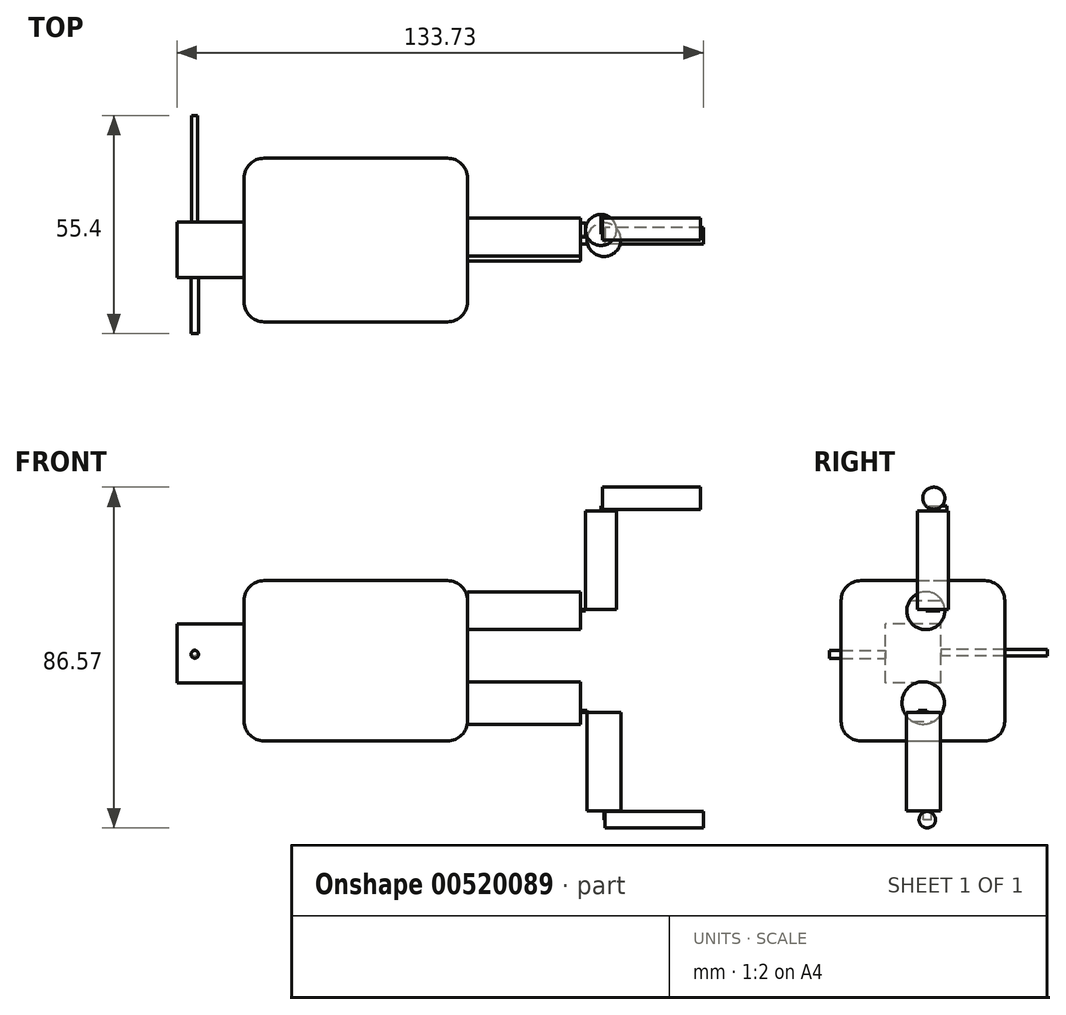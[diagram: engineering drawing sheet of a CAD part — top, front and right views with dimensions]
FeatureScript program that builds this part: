
annotation { "Feature Type Name" : "Feature", "Feature Type Description" : "" }
export const myFeature = defineFeature(function(context is Context, id is Id, definition is map)
    precondition{}
    {
        {
            var Q0;
            Q0=qCreatedBy(makeId("Top.planeOp"),FACE);
            var sketch = newSketch(context, id + "F0", { "sketchPlane" : qUnion([Q0])});
            skLineSegment(sketch, "E0.bottom", {"start": v(-23.58, -17.27) * mm, "end": v(33.13, -17.27) * mm});
            skLineSegment(sketch, "E0.top", {"start": v(-23.58, 24.28) * mm, "end": v(33.13, 24.28) * mm});
            skLineSegment(sketch, "E0.left", {"start": v(-23.58, -17.27) * mm, "end": v(-23.58, 24.28) * mm});
            skLineSegment(sketch, "E0.right", {"start": v(33.13, -17.27) * mm, "end": v(33.13, 24.28) * mm});
            skSolve(sketch);
        }
        {
            var Q0;
            Q0=makeQuery(id+"F0.imprint","IMPRINT",FACE,{"disambiguationData":[TD([[makeQuery(id+"F0.imprint","IMPRINT",EDGE,{"derivedFrom":sQuery(id+"F0.wireOp",EDGE,"E0.bottom")}),1.0]])]});
            extrude(context, id + "F1", {"entities" : qUnion([Q0]), "depth" : 40.7 * mm});
        }
        {
            var Q0;
            Q0=makeQuery(id+"F1.opExtrude","SWEPT_EDGE",EDGE,{"disambiguationData":[OSD([sQuery(id+"F0.wireOp",EDGE,"E0.top"),sQuery(id+"F0.wireOp",EDGE,"E0.left")])]});
            var Q1;
            Q1=makeQuery(id+"F1.opExtrude","CAP_EDGE",EDGE,{"disambiguationData":[OSD([sQuery(id+"F0.wireOp",EDGE,"E0.top")])],"isStart":true});
            var Q2;
            Q2=makeQuery(id+"F1.opExtrude","CAP_EDGE",EDGE,{"disambiguationData":[OSD([sQuery(id+"F0.wireOp",EDGE,"E0.left")])],"isStart":true});
            var Q3;
            Q3=makeQuery(id+"F1.opExtrude","CAP_EDGE",EDGE,{"disambiguationData":[OSD([sQuery(id+"F0.wireOp",EDGE,"E0.top")])],"isStart":false});
            var Q4;
            Q4=makeQuery(id+"F1.opExtrude","SWEPT_EDGE",EDGE,{"disambiguationData":[OSD([sQuery(id+"F0.wireOp",EDGE,"E0.top"),sQuery(id+"F0.wireOp",EDGE,"E0.right")])]});
            var Q5;
            Q5=makeQuery(id+"F1.opExtrude","CAP_EDGE",EDGE,{"disambiguationData":[OSD([sQuery(id+"F0.wireOp",EDGE,"E0.left")])],"isStart":false});
            var Q6;
            Q6=makeQuery(id+"F1.opExtrude","CAP_EDGE",EDGE,{"disambiguationData":[OSD([sQuery(id+"F0.wireOp",EDGE,"E0.right")])],"isStart":false});
            var Q7;
            Q7=makeQuery(id+"F1.opExtrude","SWEPT_EDGE",EDGE,{"disambiguationData":[OSD([sQuery(id+"F0.wireOp",EDGE,"E0.bottom"),sQuery(id+"F0.wireOp",EDGE,"E0.left")])]});
            var Q8;
            Q8=makeQuery(id+"F1.opExtrude","CAP_EDGE",EDGE,{"disambiguationData":[OSD([sQuery(id+"F0.wireOp",EDGE,"E0.bottom")])],"isStart":false});
            var Q9;
            Q9=makeQuery(id+"F1.opExtrude","CAP_EDGE",EDGE,{"disambiguationData":[OSD([sQuery(id+"F0.wireOp",EDGE,"E0.right")])],"isStart":true});
            var Q10;
            Q10=makeQuery(id+"F1.opExtrude","CAP_EDGE",EDGE,{"disambiguationData":[OSD([sQuery(id+"F0.wireOp",EDGE,"E0.bottom")])],"isStart":true});
            var Q11;
            Q11=makeQuery(id+"F1.opExtrude","SWEPT_EDGE",EDGE,{"disambiguationData":[OSD([sQuery(id+"F0.wireOp",EDGE,"E0.bottom"),sQuery(id+"F0.wireOp",EDGE,"E0.right")])]});
            fillet(context, id + "F2", {"entities" : qUnion([Q0, Q1, Q2, Q3, Q4, Q5, Q6, Q7, Q8, Q9, Q10, Q11]), "radius" : 5 * mm, "tangentPropagation" : true, "allowEdgeOverflow" : false});
        }
        {
            var Q0;
            Q0=makeQuery(id+"F1.opExtrude","SWEPT_FACE",FACE,{"disambiguationData":[OSD([sQuery(id+"F0.wireOp",EDGE,"E0.left")])]});
            var sketch = newSketch(context, id + "F3", { "sketchPlane" : qUnion([Q0])});
            skLineSegment(sketch, "E1.bottom", {"start": v(-8.11, 14.74) * mm, "end": v(5.98, 14.74) * mm});
            skLineSegment(sketch, "E1.top", {"start": v(-8.11, 29.69) * mm, "end": v(5.98, 29.69) * mm});
            skLineSegment(sketch, "E1.left", {"start": v(-8.11, 14.74) * mm, "end": v(-8.11, 29.69) * mm});
            skLineSegment(sketch, "E1.right", {"start": v(5.98, 14.74) * mm, "end": v(5.98, 29.69) * mm});
            skSolve(sketch);
        }
        {
            var Q0;
            Q0=makeQuery(id+"F3.imprint","IMPRINT",FACE,{"disambiguationData":[TD([[makeQuery(id+"F3.imprint","IMPRINT",EDGE,{"derivedFrom":sQuery(id+"F3.wireOp",EDGE,"E1.bottom")}),1.0]])]});
            extrude(context, id + "F4", {"entities" : qUnion([Q0]), "operationType" : NewBodyOperationType.ADD, "depth" : 17.1 * mm});
        }
        {
            var Q0;
            Q0=makeQuery(id+"F4.opExtrude","SWEPT_FACE",FACE,{"disambiguationData":[OSD([sQuery(id+"F3.wireOp",EDGE,"E1.right")])]});
            var sketch = newSketch(context, id + "F5", { "sketchPlane" : qUnion([Q0])});
            skCircle(sketch, "E2", {"center": v(-36.21, 22.4) * mm, "radius": 0.8 * mm});
            skSolve(sketch);
        }
        {
            var Q0;
            Q0=makeQuery(id+"F5.imprint","IMPRINT",FACE,{"disambiguationData":[TD([[makeQuery(id+"F5.imprint","IMPRINT",EDGE,{"derivedFrom":sQuery(id+"F5.wireOp",EDGE,"E2")}),1.0]])]});
            extrude(context, id + "F6", {"entities" : qUnion([Q0]), "operationType" : NewBodyOperationType.ADD, "oppositeDirection" : true, "depth" : 41.1 * mm});
        }
        {
            var Q0;
            Q0=makeQuery(id+"F4.opExtrude","SWEPT_FACE",FACE,{"disambiguationData":[OSD([sQuery(id+"F3.wireOp",EDGE,"E1.right")])]});
            var sketch = newSketch(context, id + "F7", { "sketchPlane" : qUnion([Q0])});
            skCircle(sketch, "E3", {"center": v(-36.13, 21.96) * mm, "radius": 0.97 * mm});
            skSolve(sketch);
        }
        {
            var Q0;
            Q0=makeQuery(id+"F7.imprint","IMPRINT",FACE,{"disambiguationData":[TD([[makeQuery(id+"F7.imprint","IMPRINT",EDGE,{"derivedFrom":sQuery(id+"F7.wireOp",EDGE,"E3")}),1.0]])]});
            extrude(context, id + "F8", {"entities" : qUnion([Q0]), "operationType" : NewBodyOperationType.ADD, "depth" : 14.3 * mm});
        }
        {
            var Q0;
            Q0=makeQuery(id+"F8.opExtrude","CAP_FACE",FACE,{"disambiguationData":[OSD([sQuery(id+"F7.wireOp",EDGE,"E3")])],"isStart":false});
            var sketch = newSketch(context, id + "F9", { "sketchPlane" : qUnion([Q0])});
            skArc(sketch, "E4", {"start": v(-36.1, 22.93) * mm, "mid": v(-44.04, 23.01) * mm, "end": v(-36.35, 21.02) * mm});
            skSolve(sketch);
        }
        {
            var Q0;
            Q0=makeQuery(id+"F1.opExtrude","SWEPT_FACE",FACE,{"disambiguationData":[OSD([sQuery(id+"F0.wireOp",EDGE,"E0.right")])]});
            var sketch = newSketch(context, id + "F10", { "sketchPlane" : qUnion([Q0])});
            skCircle(sketch, "E5", {"center": v(4.26, 33.07) * mm, "radius": 4.81 * mm});
            skCircle(sketch, "E6", {"center": v(3.57, 9.63) * mm, "radius": 5.4 * mm});
            skSolve(sketch);
        }
        {
            var Q0;
            Q0=qSketchRegion(id+"F10",true);
            extrude(context, id + "F11", {"entities" : qUnion([Q0]), "operationType" : NewBodyOperationType.ADD, "depth" : 28.7 * mm});
        }
        {
            var Q0;
            Q0=makeQuery(id+"F11.opExtrude","CAP_FACE",FACE,{"disambiguationData":[OSD([sQuery(id+"F10.wireOp",EDGE,"E5")])],"isStart":false});
            var sketch = newSketch(context, id + "F12", { "sketchPlane" : qUnion([Q0])});
            skLineSegment(sketch, "E7.bottom", {"start": v(4.26, 33.07) * mm, "end": v(7.84, 33.07) * mm});
            skLineSegment(sketch, "E7.top", {"start": v(4.26, 33.43) * mm, "end": v(7.84, 33.43) * mm});
            skLineSegment(sketch, "E7.left", {"start": v(4.26, 33.07) * mm, "end": v(4.26, 33.43) * mm});
            skLineSegment(sketch, "E7.right", {"start": v(7.84, 33.07) * mm, "end": v(7.84, 33.43) * mm});
            skSolve(sketch);
        }
        {
            var Q0;
            Q0=qSketchRegion(id+"F12",true);
            extrude(context, id + "F13", {"entities" : qUnion([Q0]), "operationType" : NewBodyOperationType.ADD, "depth" : 1.3 * mm});
        }
        {
            var Q0;
            Q0=makeQuery(id+"F13.opExtrude","SWEPT_FACE",FACE,{"disambiguationData":[OSD([sQuery(id+"F12.wireOp",EDGE,"E7.top")])]});
            var sketch = newSketch(context, id + "F14", { "sketchPlane" : qUnion([Q0])});
            skCircle(sketch, "E8", {"center": v(67.07, 6.05) * mm, "radius": 3.94 * mm});
            skPoint(sketch, "E8.first.point", {"position": v(63.13, 6.05) * mm});
            skPoint(sketch, "E8.second.point", {"position": v(71, 6.05) * mm});
            skPoint(sketch, "E8.second.point.positionSnap0", {"position": v(63.13, 6.05) * mm});
            skPoint(sketch, "E8.third.point", {"position": v(68.36, 9.77) * mm});
            skSolve(sketch);
        }
        {
            var Q0;
            Q0=qSketchRegion(id+"F14",true);
            extrude(context, id + "F15", {"entities" : qUnion([Q0]), "depth" : 25 * mm});
        }
        {
            var Q0;
            Q0=makeQuery(id+"F11.opExtrude","CAP_FACE",FACE,{"disambiguationData":[OSD([sQuery(id+"F10.wireOp",EDGE,"E6")])],"isStart":false});
            var sketch = newSketch(context, id + "F16", { "sketchPlane" : qUnion([Q0])});
            skLineSegment(sketch, "E9.bottom", {"start": v(2.43, 7.17) * mm, "end": v(4.59, 7.17) * mm});
            skLineSegment(sketch, "E9.top", {"start": v(2.43, 7.74) * mm, "end": v(4.59, 7.74) * mm});
            skLineSegment(sketch, "E9.left", {"start": v(2.43, 7.17) * mm, "end": v(2.43, 7.74) * mm});
            skLineSegment(sketch, "E9.right", {"start": v(4.59, 7.17) * mm, "end": v(4.59, 7.74) * mm});
            skSolve(sketch);
        }
        {
            var Q0;
            Q0=qSketchRegion(id+"F16",true);
            extrude(context, id + "F17", {"entities" : qUnion([Q0]), "operationType" : NewBodyOperationType.ADD, "depth" : 1.7 * mm});
        }
        {
            var Q0;
            Q0=makeQuery(id+"F17.opExtrude","SWEPT_FACE",FACE,{"disambiguationData":[OSD([sQuery(id+"F16.wireOp",EDGE,"E9.bottom")])]});
            var sketch = newSketch(context, id + "F18", { "sketchPlane" : qUnion([Q0])});
            skCircle(sketch, "E10", {"center": v(67.82, -3.61) * mm, "radius": 4.3 * mm});
            skPoint(sketch, "E10.first.point", {"position": v(63.53, -3.5) * mm});
            skPoint(sketch, "E10.second.point", {"position": v(72.1, -3.5) * mm});
            skPoint(sketch, "E10.second.point.positionSnap0", {"position": v(63.53, -3.5) * mm});
            skPoint(sketch, "E10.third.point", {"position": v(68.95, 0.53) * mm});
            skSolve(sketch);
        }
        {
            var Q0;
            Q0=qSketchRegion(id+"F18",true);
            extrude(context, id + "F19", {"entities" : qUnion([Q0]), "operationType" : NewBodyOperationType.ADD, "depth" : 25 * mm});
        }
        {
            var Q0;
            Q0=makeQuery(id+"F19.opExtrude","CAP_FACE",FACE,{"disambiguationData":[OSD([sQuery(id+"F18.wireOp",EDGE,"E10")])],"isStart":false});
            var sketch = newSketch(context, id + "F20", { "sketchPlane" : qUnion([Q0])});
            skLineSegment(sketch, "E11.bottom", {"start": v(68.05, -5.63) * mm, "end": v(67.82, -5.63) * mm});
            skLineSegment(sketch, "E11.top", {"start": v(68.05, -3.61) * mm, "end": v(67.82, -3.61) * mm});
            skLineSegment(sketch, "E11.left", {"start": v(68.05, -5.63) * mm, "end": v(68.05, -3.61) * mm});
            skLineSegment(sketch, "E11.right", {"start": v(67.82, -5.63) * mm, "end": v(67.82, -3.61) * mm});
            skSolve(sketch);
        }
        {
            var Q0;
            Q0=qSketchRegion(id+"F20",true);
            extrude(context, id + "F21", {"entities" : qUnion([Q0]), "operationType" : NewBodyOperationType.ADD, "depth" : 2.2 * mm});
        }
        {
            var Q0;
            Q0=makeQuery(id+"F21.opExtrude","SWEPT_FACE",FACE,{"disambiguationData":[OSD([sQuery(id+"F20.wireOp",EDGE,"E11.left")])]});
            var sketch = newSketch(context, id + "F22", { "sketchPlane" : qUnion([Q0])});
            skCircle(sketch, "E12", {"center": v(4.62, -20.03) * mm, "radius": 2.08 * mm});
            skSolve(sketch);
        }
        {
            var Q0;
            Q0=qSketchRegion(id+"F22",true);
            extrude(context, id + "F23", {"entities" : qUnion([Q0]), "operationType" : NewBodyOperationType.ADD, "depth" : 25 * mm});
        }
        {
            var Q0;
            Q0=makeQuery(id+"F15.opExtrude","CAP_FACE",FACE,{"disambiguationData":[OSD([sQuery(id+"F14.wireOp",EDGE,"E8")])],"isStart":false});
            var sketch = newSketch(context, id + "F24", { "sketchPlane" : qUnion([Q0])});
            skLineSegment(sketch, "E13.bottom", {"start": v(67.12, 5.02) * mm, "end": v(67.38, 5.02) * mm});
            skLineSegment(sketch, "E13.top", {"start": v(67.12, 9.6) * mm, "end": v(67.38, 9.6) * mm});
            skLineSegment(sketch, "E13.left", {"start": v(67.12, 5.02) * mm, "end": v(67.12, 9.6) * mm});
            skLineSegment(sketch, "E13.right", {"start": v(67.38, 5.02) * mm, "end": v(67.38, 9.6) * mm});
            skSolve(sketch);
        }
        {
            var Q0;
            Q0=qSketchRegion(id+"F24",true);
            extrude(context, id + "F25", {"entities" : qUnion([Q0]), "operationType" : NewBodyOperationType.ADD, "depth" : 1.2 * mm});
        }
        {
            var Q0;
            Q0=makeQuery(id+"F25.opExtrude","SWEPT_FACE",FACE,{"disambiguationData":[OSD([sQuery(id+"F24.wireOp",EDGE,"E13.right")])]});
            var sketch = newSketch(context, id + "F26", { "sketchPlane" : qUnion([Q0])});
            skCircle(sketch, "E14", {"center": v(6.29, 61.66) * mm, "radius": 2.8 * mm});
            skPoint(sketch, "E14.first.point", {"position": v(6.68, 58.88) * mm});
            skPoint(sketch, "E14.second.point", {"position": v(6.47, 64.46) * mm});
            skPoint(sketch, "E14.third.point", {"position": v(9.09, 61.8) * mm});
            skSolve(sketch);
        }
        {
            var Q0;
            Q0=qSketchRegion(id+"F26",true);
            extrude(context, id + "F27", {"entities" : qUnion([Q0]), "operationType" : NewBodyOperationType.ADD, "depth" : 25 * mm});
        }
    });
